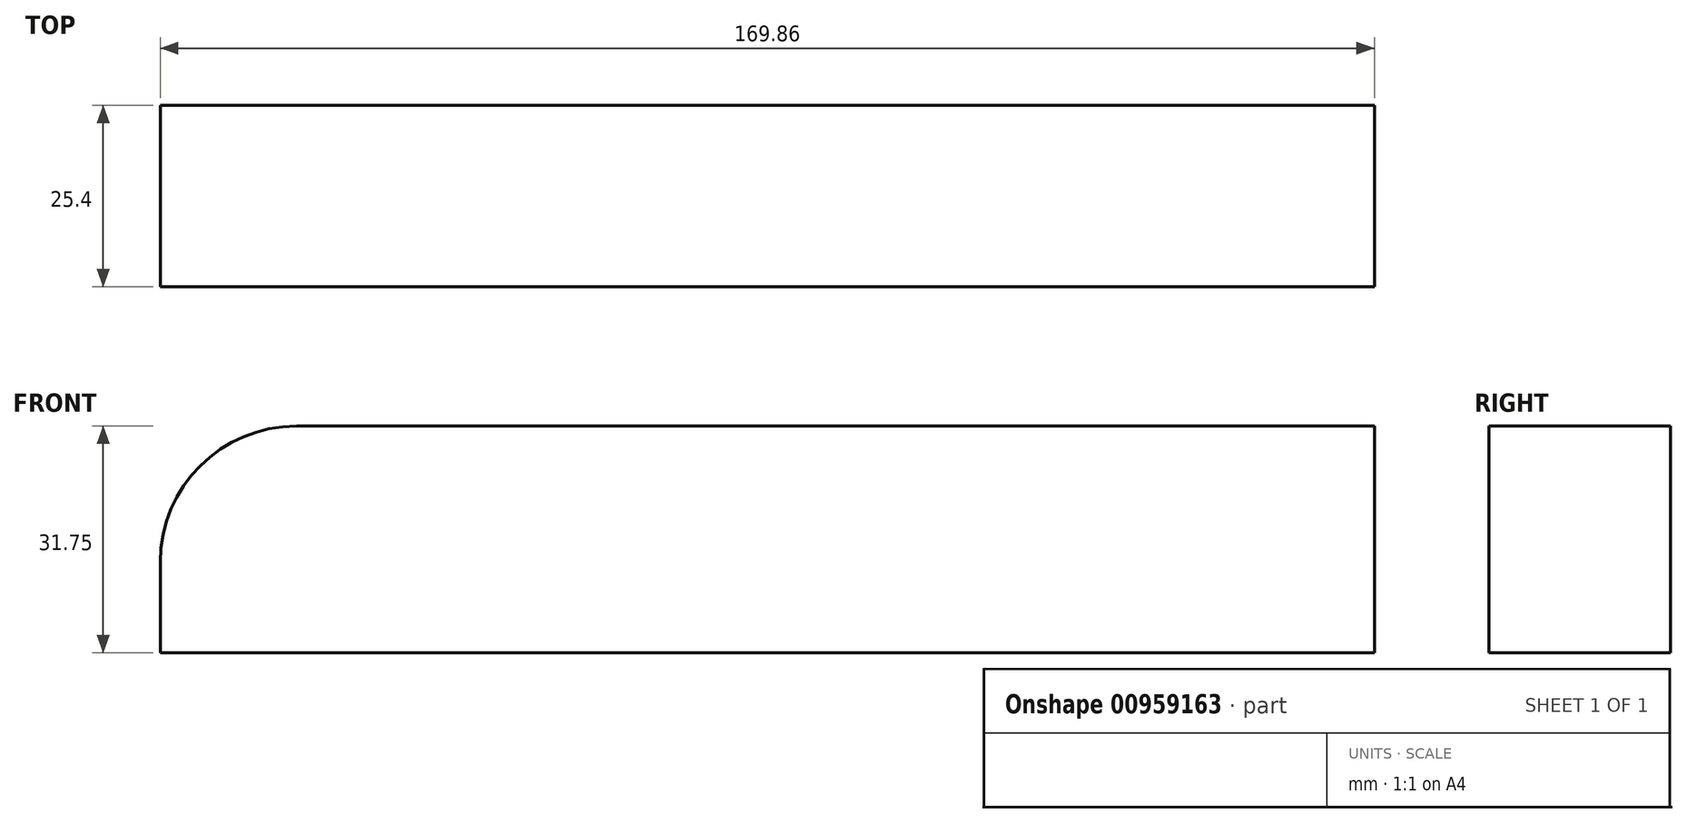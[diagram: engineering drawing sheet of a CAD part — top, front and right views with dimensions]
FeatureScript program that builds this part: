
annotation { "Feature Type Name" : "Feature", "Feature Type Description" : "" }
export const myFeature = defineFeature(function(context is Context, id is Id, definition is map)
    precondition{}
    {
        {
            var Q0;
            Q0=qCreatedBy(makeId("Front.planeOp"),FACE);
            var sketch = newSketch(context, id + "F0", { "sketchPlane" : qUnion([Q0])});
            skLineSegment(sketch, "E0", {"start": v(0, 0) * mm, "end": v(-68.26, 0) * mm});
            skLineSegment(sketch, "E1", {"start": v(-68.26, 0) * mm, "end": v(-68.26, -50.8) * mm});
            skLineSegment(sketch, "E2", {"start": v(-68.26, -50.8) * mm, "end": v(-87.31, -50.8) * mm});
            skLineSegment(sketch, "E3", {"start": v(-87.31, -50.8) * mm, "end": v(-87.31, 0) * mm});
            skLineSegment(sketch, "E4", {"start": v(-87.31, 0) * mm, "end": v(-169.86, 0) * mm});
            skLineSegment(sketch, "E5", {"start": v(-169.86, 0) * mm, "end": v(-169.86, 12.7) * mm});
            skLineSegment(sketch, "E6", {"start": v(-150.81, 31.75) * mm, "end": v(0, 31.75) * mm});
            skLineSegment(sketch, "E7", {"start": v(0, 31.75) * mm, "end": v(0, 0) * mm});
            skLineSegment(sketch, "E8", {"start": v(-87.31, 0) * mm, "end": v(-68.26, 0) * mm});
            skPoint(sketch, "E9.visualSharp", {"position": v(-169.86, 31.75) * mm});
            skArc(sketch, "E9.filletArc", {"start": v(-150.81, 31.75) * mm, "mid": v(-164.28, 26.17) * mm, "end": v(-169.86, 12.7) * mm});
            skSolve(sketch);
        }
        {
            var Q0;
            {var subQ2=sQuery(id+"F0.wireOp",EDGE,"E6");Q0=makeQuery(id+"F0.imprint","IMPRINT",FACE,{"disambiguationData":[TD([[makeQuery(id+"F0.imprint","IMPRINT",EDGE,{"derivedFrom":subQ2}),-1.0]])]});}
            extrude(context, id + "F1", {"entities" : qUnion([Q0]), "depth" : 25.4 * mm, "offsetDistance" : 25.4 * mm});
        }
        {
            var Q0;
            {var subQ1=sQuery(id+"F0.wireOp",EDGE,"E0");Q0=makeQuery(id+"F0.imprint","IMPRINT",FACE,{"disambiguationData":[TD([[makeQuery(id+"F0.imprint","IMPRINT",EDGE,{"derivedFrom":subQ1}),-1.0]])]});}
            extrude(context, id + "F2", {"entities" : qUnion([Q0]), "depth" : 25.4 * mm, "offsetDistance" : 25.4 * mm});
        }
        {
            var Q0;
            {var subQ0=sQuery(id+"F0.wireOp",EDGE,"E5");Q0=makeQuery(id+"F0.imprint","IMPRINT",FACE,{"disambiguationData":[TD([[makeQuery(id+"F0.imprint","IMPRINT",EDGE,{"derivedFrom":subQ0}),-1.0]])]});}
            extrude(context, id + "F3", {"entities" : qUnion([Q0]), "depth" : 25.4 * mm, "offsetDistance" : 25.4 * mm});
        }
    });
